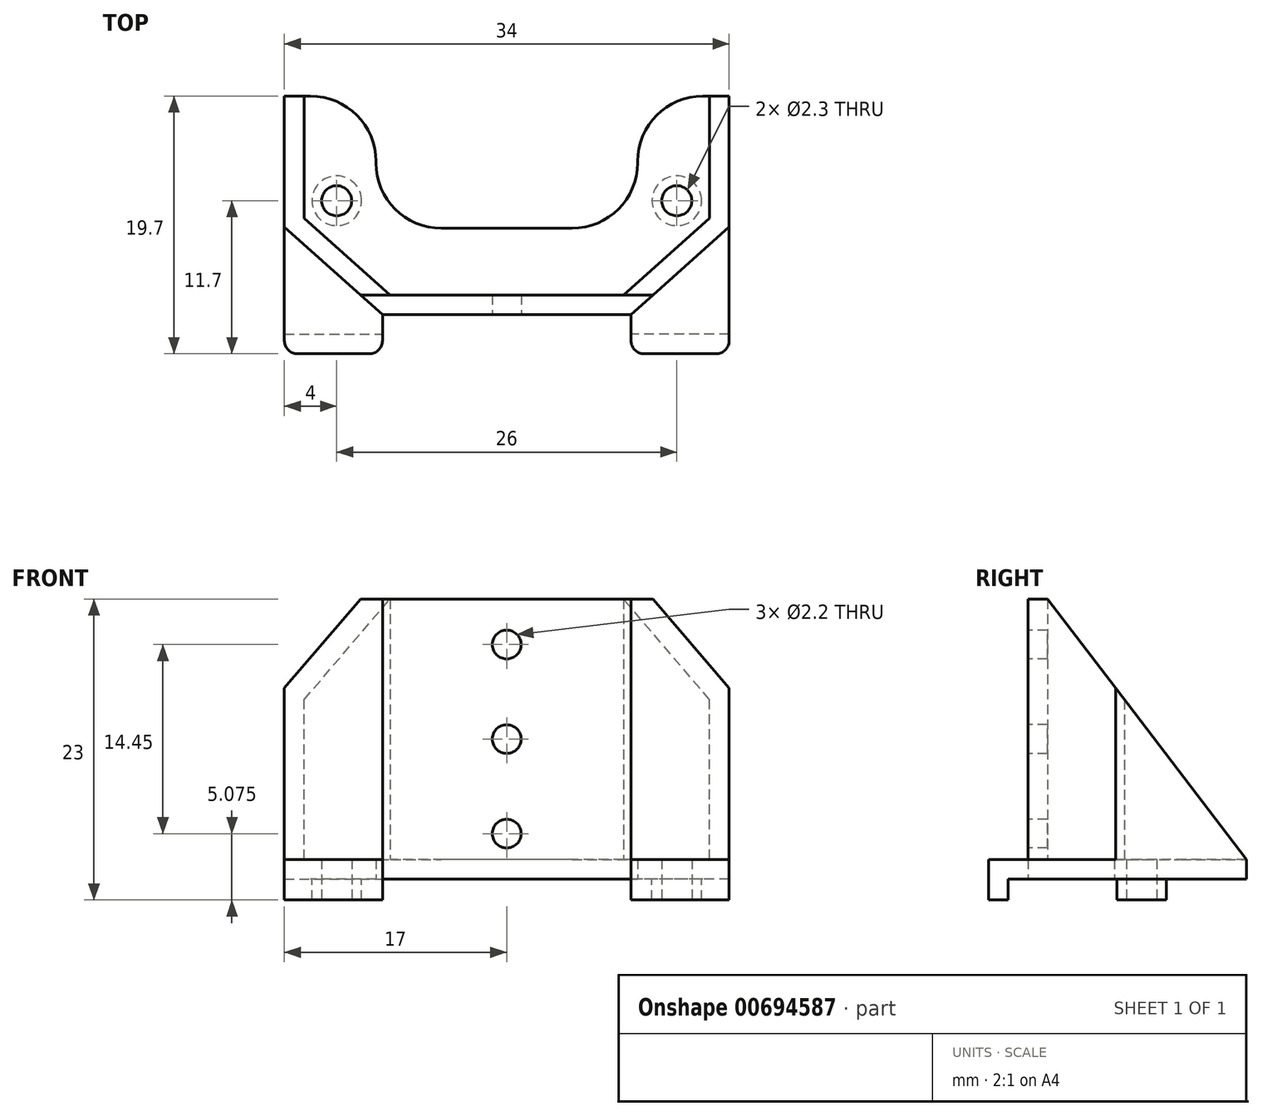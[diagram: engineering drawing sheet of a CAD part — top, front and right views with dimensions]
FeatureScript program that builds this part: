
annotation { "Feature Type Name" : "Feature", "Feature Type Description" : "" }
export const myFeature = defineFeature(function(context is Context, id is Id, definition is map)
    precondition{}
    {
        {
            var Q0;
            Q0=qCreatedBy(makeId("Top.planeOp"),FACE);
            var sketch = newSketch(context, id + "F0", { "sketchPlane" : qUnion([Q0])});
            skLineSegment(sketch, "E0", {"start": v(-15, -8.1) * mm, "end": v(15, -8.1) * mm});
            skLineSegment(sketch, "E1.bottom", {"start": v(-15, 24) * mm, "end": v(-11, 24) * mm});
            skLineSegment(sketch, "E1.top", {"start": v(-15, 0) * mm, "end": v(-11, 0) * mm});
            skLineSegment(sketch, "E1.left", {"start": v(-15, 24) * mm, "end": v(-15, 0) * mm});
            skLineSegment(sketch, "E1.right", {"start": v(-11, 24) * mm, "end": v(-11, 0) * mm});
            skLineSegment(sketch, "E2.MirrorCS", {"start": v(11, 24) * mm, "end": v(11, 0) * mm});
            skLineSegment(sketch, "E3.MirrorCS", {"start": v(15, 24) * mm, "end": v(15, 0) * mm});
            skLineSegment(sketch, "E4.MirrorCS", {"start": v(15, 24) * mm, "end": v(11, 24) * mm});
            skLineSegment(sketch, "E5.MirrorCS", {"start": v(15, 0) * mm, "end": v(11, 0) * mm});
            skSolve(sketch);
        }
        {
            var Q0;
            Q0=qCreatedBy(makeId("Top.planeOp"),FACE);
            var sketch = newSketch(context, id + "F1", { "sketchPlane" : qUnion([Q0])});
            skCircle(sketch, "E6", {"center": v(-13, 2) * mm, "radius": 1.9 * mm});
            skCircle(sketch, "E7.MirrorC", {"center": v(13, 2) * mm, "radius": 1.9 * mm});
            skLineSegment(sketch, "E8.bottom", {"start": v(-9.5, -8.2) * mm, "end": v(9.5, -8.2) * mm, "construction": true});
            skLineSegment(sketch, "E8.top", {"start": v(-9.5, -9.7) * mm, "end": v(9.5, -9.7) * mm, "construction": true});
            skLineSegment(sketch, "E8.left", {"start": v(-9.5, -8.2) * mm, "end": v(-9.5, -9.7) * mm, "construction": true});
            skLineSegment(sketch, "E8.right", {"start": v(9.5, -8.2) * mm, "end": v(9.5, -9.7) * mm, "construction": true});
            skSolve(sketch);
        }
        {
            var Q0;
            Q0=qCreatedBy(makeId("Top.planeOp"),FACE);
            var sketch = newSketch(context, id + "F2", { "sketchPlane" : qUnion([Q0])});
            skLineSegment(sketch, "E9", {"start": v(-9.5, -6.7) * mm, "end": v(-17, 0) * mm});
            skLineSegment(sketch, "E10", {"start": v(-17, 0) * mm, "end": v(-17, 10) * mm});
            skLineSegment(sketch, "E11", {"start": v(-17, 10) * mm, "end": v(-10, 10) * mm});
            skLineSegment(sketch, "E12", {"start": v(-10, 10) * mm, "end": v(-10, -0.1) * mm});
            skLineSegment(sketch, "E13", {"start": v(-10, -0.1) * mm, "end": v(0, -0.1) * mm});
            skLineSegment(sketch, "E14", {"start": v(-9.5, -6.7) * mm, "end": v(0, -6.7) * mm});
            skLineSegment(sketch, "E15.MirrorCS", {"start": v(10, -0.1) * mm, "end": v(0, -0.1) * mm});
            skLineSegment(sketch, "E16.MirrorCS", {"start": v(10, 10) * mm, "end": v(10, -0.1) * mm});
            skLineSegment(sketch, "E17.MirrorCS", {"start": v(17, 10) * mm, "end": v(10, 10) * mm});
            skLineSegment(sketch, "E18.MirrorCS", {"start": v(17, 0) * mm, "end": v(17, 10) * mm});
            skLineSegment(sketch, "E19.MirrorCS", {"start": v(9.5, -6.7) * mm, "end": v(17, 0) * mm});
            skLineSegment(sketch, "E20.MirrorCS", {"start": v(9.5, -6.7) * mm, "end": v(0, -6.7) * mm});
            skSolve(sketch);
        }
        {
            var Q0;
            Q0=makeQuery(id+"F2.imprint","IMPRINT",FACE,{"disambiguationData":[TD([[makeQuery(id+"F2.imprint","IMPRINT",EDGE,{"derivedFrom":sQuery(id+"F2.wireOp",EDGE,"E9")}),-1.0]])]});
            var sketch = newSketch(context, id + "F3", { "sketchPlane" : qUnion([Q0])});
            skLineSegment(sketch, "E21", {"start": v(-17, 10) * mm, "end": v(-17, 0) * mm});
            skLineSegment(sketch, "E22", {"start": v(-17, 0) * mm, "end": v(-9.5, -6.7) * mm});
            skLineSegment(sketch, "E23", {"start": v(-9.5, -6.7) * mm, "end": v(0, -6.7) * mm});
            skLineSegment(sketch, "E24", {"start": v(-17, 10) * mm, "end": v(-15.5, 10) * mm});
            skLineSegment(sketch, "E25", {"start": v(-15.5, 10) * mm, "end": v(-15.5, 0.67) * mm});
            skLineSegment(sketch, "E26", {"start": v(-15.5, 0.67) * mm, "end": v(-8.93, -5.2) * mm});
            skLineSegment(sketch, "E27", {"start": v(-8.93, -5.2) * mm, "end": v(0, -5.2) * mm});
            skPoint(sketch, "E28.orphan", {"position": v(-15.5, 0) * mm});
            skLineSegment(sketch, "E29.MirrorCS", {"start": v(15.5, 10) * mm, "end": v(15.5, 0.67) * mm});
            skLineSegment(sketch, "E30.MirrorCS", {"start": v(17, 10) * mm, "end": v(17, 0) * mm});
            skLineSegment(sketch, "E31.MirrorCS", {"start": v(17, 0) * mm, "end": v(9.5, -6.7) * mm});
            skLineSegment(sketch, "E32.MirrorCS", {"start": v(9.5, -6.7) * mm, "end": v(0, -6.7) * mm});
            skLineSegment(sketch, "E33.MirrorCS", {"start": v(8.93, -5.2) * mm, "end": v(0, -5.2) * mm});
            skLineSegment(sketch, "E34.MirrorCS", {"start": v(15.5, 0.67) * mm, "end": v(8.93, -5.2) * mm});
            skLineSegment(sketch, "E35.MirrorCS", {"start": v(17, 10) * mm, "end": v(15.5, 10) * mm});
            skSolve(sketch);
        }
        {
            var Q0;
            Q0=qSketchRegion(id+"F3",true);
            extrude(context, id + "F4", {"entities" : qUnion([Q0]), "depth" : 21.4 * mm, "offsetDistance" : 25 * mm});
        }
        {
            var Q0;
            Q0=qSketchRegion(id+"F2",true);
            extrude(context, id + "F5", {"entities" : qUnion([Q0]), "operationType" : NewBodyOperationType.ADD, "depth" : 1.5 * mm, "offsetDistance" : 25 * mm});
        }
        {
            var Q0;
            Q0=qSketchRegion(id+"F1",true);
            extrude(context, id + "F6", {"entities" : qUnion([Q0]), "operationType" : NewBodyOperationType.ADD, "oppositeDirection" : true, "depth" : 1.6 * mm, "offsetDistance" : 25 * mm});
        }
        {
            var Q0;
            Q0=qCreatedBy(makeId("Right.planeOp"),FACE);
            var sketch = newSketch(context, id + "F7", { "sketchPlane" : qUnion([Q0])});
            skLineSegment(sketch, "E36", {"start": v(10, 1.5) * mm, "end": v(-5.2, 21.4) * mm});
            skLineSegment(sketch, "E37", {"start": v(-5.2, 21.4) * mm, "end": v(10, 21.4) * mm});
            skLineSegment(sketch, "E38", {"start": v(10, 21.4) * mm, "end": v(10, 1.5) * mm});
            skSolve(sketch);
        }
        {
            var Q0;
            Q0=qSketchRegion(id+"F7",true);
            extrude(context, id + "F8", {"entities" : qUnion([Q0]), "operationType" : NewBodyOperationType.REMOVE, "endBound" : BoundingType.THROUGH_ALL, "oppositeDirection" : true, "depth" : 25 * mm, "offsetDistance" : 25 * mm, "hasSecondDirection" : true, "secondDirectionBound" : SecondDirectionBoundingType.THROUGH_ALL, "secondDirectionOppositeDirection" : false, "secondDirectionDepth" : 25 * mm});
        }
        {
            var Q0;
            Q0=qCreatedBy(makeId("Top.planeOp"),FACE);
            var sketch = newSketch(context, id + "F9", { "sketchPlane" : qUnion([Q0])});
            skCircle(sketch, "E39", {"center": v(13, 2) * mm, "radius": 1.15 * mm});
            skCircle(sketch, "E40.MirrorC", {"center": v(-13, 2) * mm, "radius": 1.15 * mm});
            skSolve(sketch);
        }
        {
            var Q0;
            Q0=qSketchRegion(id+"F9",true);
            extrude(context, id + "F10", {"entities" : qUnion([Q0]), "operationType" : NewBodyOperationType.REMOVE, "endBound" : BoundingType.THROUGH_ALL, "depth" : 25 * mm, "offsetDistance" : 25 * mm, "hasSecondDirection" : true, "secondDirectionBound" : SecondDirectionBoundingType.THROUGH_ALL, "secondDirectionOppositeDirection" : true, "secondDirectionDepth" : 25 * mm});
        }
        {
            var Q0;
            Q0=makeQuery(id+"F4.opExtrude","SWEPT_FACE",FACE,{"disambiguationData":[OSD([sQuery(id+"F3.wireOp",EDGE,"E23"),sQuery(id+"F3.wireOp",EDGE,"E32.MirrorCS")])]});
            var sketch = newSketch(context, id + "F11", { "sketchPlane" : qUnion([Q0])});
            skCircle(sketch, "E41", {"center": v(0, 3.47) * mm, "radius": 1.1 * mm});
            skCircle(sketch, "E42", {"center": v(0, 17.92) * mm, "radius": 1.1 * mm});
            skCircle(sketch, "E43", {"center": v(0, 10.7) * mm, "radius": 1.1 * mm});
            skSolve(sketch);
        }
        {
            var Q0;
            Q0=qSketchRegion(id+"F11",true);
            extrude(context, id + "F12", {"entities" : qUnion([Q0]), "operationType" : NewBodyOperationType.REMOVE, "endBound" : BoundingType.UP_TO_NEXT, "oppositeDirection" : true, "depth" : 25 * mm, "offsetDistance" : 25 * mm});
        }
        {
            var Q0;
            Q0=qCreatedBy(makeId("Top.planeOp"),FACE);
            var sketch = newSketch(context, id + "F13", { "sketchPlane" : qUnion([Q0])});
            skLineSegment(sketch, "E44.bottom", {"start": v(-17, -9.7) * mm, "end": v(-9.5, -9.7) * mm});
            skLineSegment(sketch, "E44.left", {"start": v(-17, -9.7) * mm, "end": v(-17, 0) * mm});
            skLineSegment(sketch, "E44.right", {"start": v(-9.5, -9.7) * mm, "end": v(-9.5, -6.7) * mm});
            skLineSegment(sketch, "E45.MirrorCS", {"start": v(17, -9.7) * mm, "end": v(9.5, -9.7) * mm});
            skLineSegment(sketch, "E46.MirrorCS", {"start": v(17, -9.7) * mm, "end": v(17, 0) * mm});
            skLineSegment(sketch, "E47.MirrorCS", {"start": v(9.5, -9.7) * mm, "end": v(9.5, -6.7) * mm});
            skLineSegment(sketch, "E48", {"start": v(-17, 0) * mm, "end": v(-9.5, -6.7) * mm});
            skPoint(sketch, "E49.orphan", {"position": v(-9.5, 0) * mm});
            skPoint(sketch, "E50.MirrorCS.end.orphan", {"position": v(9.5, 0) * mm});
            skPoint(sketch, "E50.MirrorCS.start.orphan", {"position": v(17, 0) * mm});
            skLineSegment(sketch, "E51.MirrorCS", {"start": v(17, 0) * mm, "end": v(9.5, -6.7) * mm});
            skSolve(sketch);
        }
        {
            var Q0;
            Q0=makeQuery(id+"F13.imprint","IMPRINT",FACE,{"disambiguationData":[TD([[makeQuery(id+"F13.imprint","IMPRINT",EDGE,{"derivedFrom":sQuery(id+"F13.wireOp",EDGE,"E44.bottom")}),1.0]])]});
            var sketch = newSketch(context, id + "F14", { "sketchPlane" : qUnion([Q0])});
            skLineSegment(sketch, "E52.bottom", {"start": v(-17, -9.7) * mm, "end": v(-9.5, -9.7) * mm});
            skLineSegment(sketch, "E52.top", {"start": v(-17, -8.2) * mm, "end": v(-9.5, -8.2) * mm});
            skLineSegment(sketch, "E52.left", {"start": v(-17, -9.7) * mm, "end": v(-17, -8.2) * mm});
            skLineSegment(sketch, "E52.right", {"start": v(-9.5, -9.7) * mm, "end": v(-9.5, -8.2) * mm});
            skLineSegment(sketch, "E53.MirrorCS", {"start": v(9.5, -9.7) * mm, "end": v(9.5, -8.2) * mm});
            skLineSegment(sketch, "E54.MirrorCS", {"start": v(17, -9.7) * mm, "end": v(17, -8.2) * mm});
            skLineSegment(sketch, "E55.MirrorCS", {"start": v(17, -8.2) * mm, "end": v(9.5, -8.2) * mm});
            skLineSegment(sketch, "E56.MirrorCS", {"start": v(17, -9.7) * mm, "end": v(9.5, -9.7) * mm});
            skSolve(sketch);
        }
        {
            var Q0;
            Q0 = qSketchRegion(id + "F13", true);
            extrude(context, id + "F15", {"entities" : qUnion([Q0]), "operationType" : NewBodyOperationType.ADD, "depth" : 1.5 * mm, "offsetDistance" : 25 * mm});
        }
        {
            var Q0;
            Q0 = qSketchRegion(id + "F14", true);
            extrude(context, id + "F16", {"entities" : qUnion([Q0]), "operationType" : NewBodyOperationType.ADD, "oppositeDirection" : true, "depth" : 1.6 * mm, "offsetDistance" : 25 * mm});
        }
        {
            var Q0;
            Q0=makeQuery(id+"F16.boolean.opBoolean","MERGE",EDGE,{"derivedFrom":[makeQuery(id+"F15.opExtrude","SWEPT_EDGE",EDGE,{"disambiguationData":[OSD([sQuery(id+"F13.wireOp",EDGE,"E45.MirrorCS"),sQuery(id+"F13.wireOp",EDGE,"E46.MirrorCS")])]}),makeQuery(id+"F16.opExtrude","SWEPT_EDGE",EDGE,{"disambiguationData":[OSD([sQuery(id+"F14.wireOp",EDGE,"E54.MirrorCS"),sQuery(id+"F14.wireOp",EDGE,"E56.MirrorCS")])]})]});
            var Q1;
            Q1=makeQuery(id+"F16.boolean.opBoolean","MERGE",EDGE,{"derivedFrom":[makeQuery(id+"F15.opExtrude","SWEPT_EDGE",EDGE,{"disambiguationData":[OSD([sQuery(id+"F13.wireOp",EDGE,"E44.bottom"),sQuery(id+"F13.wireOp",EDGE,"E44.left")])]}),makeQuery(id+"F16.opExtrude","SWEPT_EDGE",EDGE,{"disambiguationData":[OSD([sQuery(id+"F14.wireOp",EDGE,"E52.bottom"),sQuery(id+"F14.wireOp",EDGE,"E52.left")])]})]});
            var Q2;
            Q2=makeQuery(id+"F16.boolean.opBoolean","MERGE",EDGE,{"derivedFrom":[makeQuery(id+"F15.opExtrude","SWEPT_EDGE",EDGE,{"disambiguationData":[OSD([sQuery(id+"F13.wireOp",EDGE,"E44.bottom"),sQuery(id+"F13.wireOp",EDGE,"E44.right")])]}),makeQuery(id+"F16.opExtrude","SWEPT_EDGE",EDGE,{"disambiguationData":[OSD([sQuery(id+"F14.wireOp",EDGE,"E52.bottom"),sQuery(id+"F14.wireOp",EDGE,"E52.right")])]})]});
            var Q3;
            Q3=makeQuery(id+"F16.boolean.opBoolean","MERGE",EDGE,{"derivedFrom":[makeQuery(id+"F15.opExtrude","SWEPT_EDGE",EDGE,{"disambiguationData":[OSD([sQuery(id+"F13.wireOp",EDGE,"E45.MirrorCS"),sQuery(id+"F13.wireOp",EDGE,"E47.MirrorCS")])]}),makeQuery(id+"F16.opExtrude","SWEPT_EDGE",EDGE,{"disambiguationData":[OSD([sQuery(id+"F14.wireOp",EDGE,"E53.MirrorCS"),sQuery(id+"F14.wireOp",EDGE,"E56.MirrorCS")])]})]});
            fillet(context, id + "F17", {"entities" : qUnion([Q0, Q1, Q2, Q3]), "radius" : 1 * mm, "tangentPropagation" : true, "allowEdgeOverflow" : false});
        }
        {
            var Q0;
            Q0=makeQuery(id+"F5.opExtrude","SWEPT_EDGE",EDGE,{"disambiguationData":[OSD([sQuery(id+"F2.wireOp",EDGE,"E15.MirrorCS"),sQuery(id+"F2.wireOp",EDGE,"E16.MirrorCS")])]});
            var Q1;
            Q1=makeQuery(id+"F5.opExtrude","SWEPT_EDGE",EDGE,{"disambiguationData":[OSD([sQuery(id+"F2.wireOp",EDGE,"E16.MirrorCS"),sQuery(id+"F2.wireOp",EDGE,"E17.MirrorCS")])]});
            var Q2;
            Q2=makeQuery(id+"F5.opExtrude","SWEPT_EDGE",EDGE,{"disambiguationData":[OSD([sQuery(id+"F2.wireOp",EDGE,"E12"),sQuery(id+"F2.wireOp",EDGE,"E13")])]});
            var Q3;
            Q3=makeQuery(id+"F5.opExtrude","SWEPT_EDGE",EDGE,{"disambiguationData":[OSD([sQuery(id+"F2.wireOp",EDGE,"E11"),sQuery(id+"F2.wireOp",EDGE,"E12")])]});
            fillet(context, id + "F18", {"entities" : qUnion([Q0, Q1, Q2, Q3]), "radius" : 5 * mm, "tangentPropagation" : true, "allowEdgeOverflow" : false});
        }
    });
